# Revit family: LAV MARCUS BC_RFA
name_source: partatom
category: Aparatos sanitarios
units: mm (PartAtom-declared; Revit-internal decimal feet)

## family parameters
Activar corte en vistas = No
Compartido = Sí
Corte con vacíos al cargar = No
Cota de conector redondo = Usar diámetro
Mantener orientación de anotación = No
Número OmniClass = 23.45.05.14.14
Punto de cálculo de habitación = No
Se basa en plano de trabajo = Sí
Siempre vertical = Sí
Tipo de pieza = Normal
Título OmniClass = Sinks/Lavatories

## types (1)
- LV LUGANO JR
    Ceramic = Cerámica
    Comentarios de tipo = Lavabo de Bajo Cubierta con Rebosadero de 49 x 41 cm
    Descripción = Lavabo Rectangular Marcus Bajo Cubierta con Rebosadero
    Elevación por defecto = 35.0"
    Fabricante = Helvex S.A. de C.V.
    Imagen de tipo = <Ninguno>
    Materials = Cerámica porcelanizada de alto brillo.
    Modelo = LV LUGANO JR
    Warranty = Helvex, S. A. de C. V. garantiza sus productos
cerámicos como libres de defectos en materiales,
mano de obra y procesos de fabricación por un
periodo de 65 años.
En los herrajes por defectos de manufactura por 5
años.
El dispositivo TDS en el mingitorio seco por 3 años.
Tapa y asiento por un periodo de 2 años.
La vigencia de la garantía inicia a partir de la fecha
de entrega del producto al consumidor indicada en
esta Póliza de Garantía.

## geometry (parser evidence)
native form markers: Sweep x3
no freeform markers — native parametric forms only
